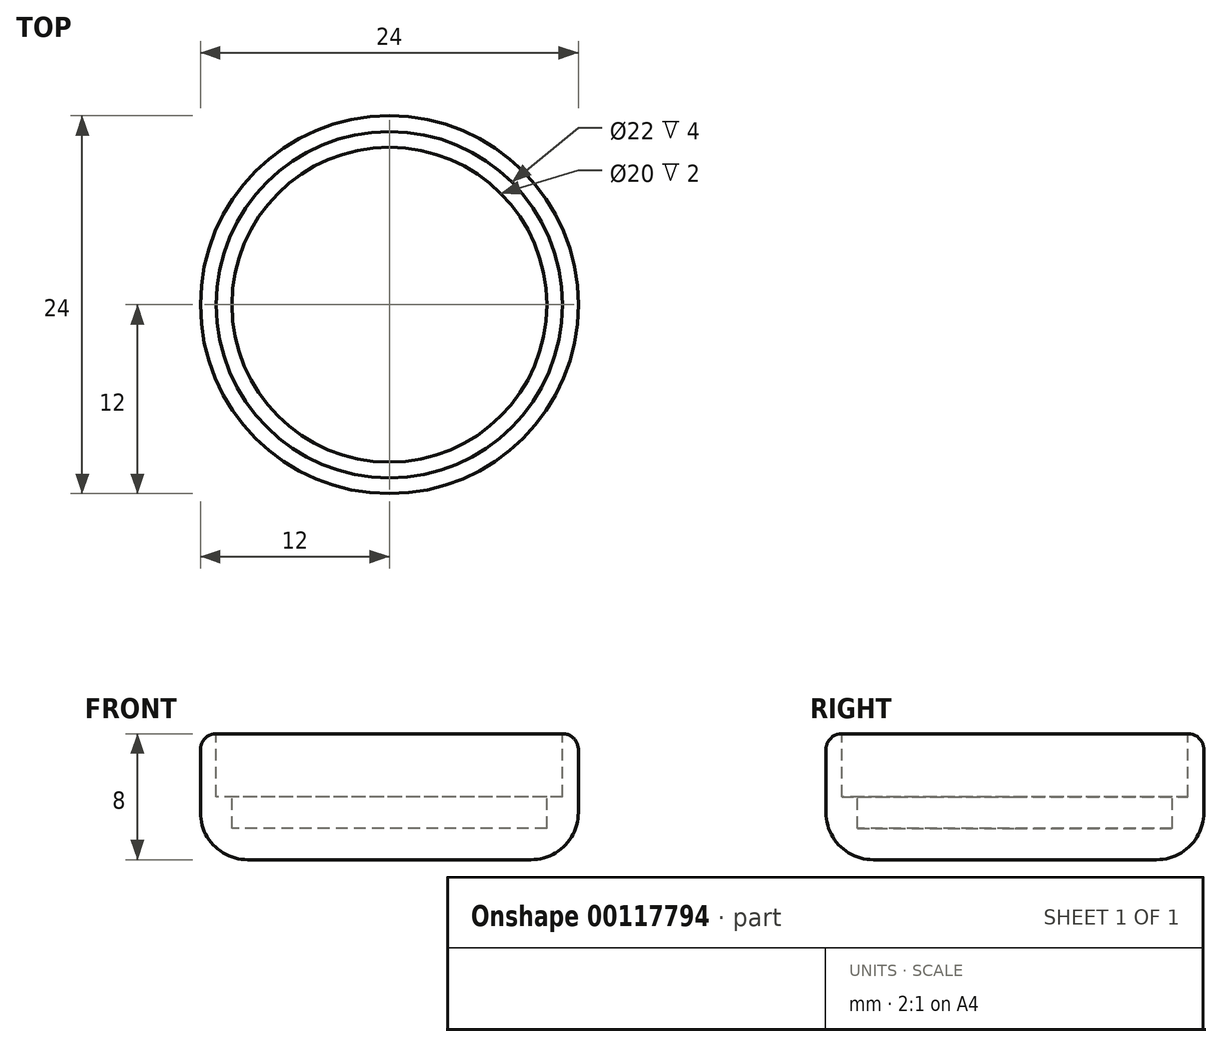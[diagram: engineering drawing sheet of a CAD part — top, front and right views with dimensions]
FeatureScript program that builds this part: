
annotation { "Feature Type Name" : "Feature", "Feature Type Description" : "" }
export const myFeature = defineFeature(function(context is Context, id is Id, definition is map)
    precondition{}
    {
        {
            var Q0;
            Q0=qCreatedBy(makeId("Top.planeOp"),FACE);
            var sketch = newSketch(context, id + "F0", { "sketchPlane" : qUnion([Q0])});
            skCircle(sketch, "E0", {"center": v(0, 0) * mm, "radius": 12 * mm});
            skSolve(sketch);
        }
        {
            var Q0;
            Q0 = qSketchRegion(id + "F0", true);
            extrude(context, id + "F1", {"entities" : qUnion([Q0]), "depth" : 8 * mm});
        }
        {
            var Q0;
            Q0=makeQuery(id+"F1.opExtrude","CAP_FACE",FACE,{"disambiguationData":[OSD([sQuery(id+"F0.wireOp",EDGE,"E0")])],"isStart":false});
            var sketch = newSketch(context, id + "F2", { "sketchPlane" : qUnion([Q0])});
            skCircle(sketch, "E1", {"center": v(0, 0) * mm, "radius": 11 * mm});
            skCircle(sketch, "E2", {"center": v(0, 0) * mm, "radius": 10 * mm});
            skSolve(sketch);
        }
        {
            var Q0;
            Q0=makeQuery(id+"F2.imprint","IMPRINT",FACE,{"disambiguationData":[TD([[makeQuery(id+"F2.imprint","IMPRINT",EDGE,{"derivedFrom":sQuery(id+"F2.wireOp",EDGE,"E2")}),1.0]])]});
            extrude(context, id + "F3", {"entities" : qUnion([Q0]), "operationType" : NewBodyOperationType.REMOVE, "oppositeDirection" : true, "depth" : 6 * mm});
        }
        {
            var Q0;
            Q0 = qSketchRegion(id + "F2", true);
            extrude(context, id + "F4", {"entities" : qUnion([Q0]), "operationType" : NewBodyOperationType.REMOVE, "oppositeDirection" : true, "depth" : 4 * mm});
        }
        {
            var Q0;
            Q0=makeQuery(id+"F1.opExtrude","CAP_EDGE",EDGE,{"disambiguationData":[OSD([sQuery(id+"F0.wireOp",EDGE,"E0")])],"isStart":true});
            fillet(context, id + "F5", {"entities" : qUnion([Q0]), "radius" : 3 * mm, "tangentPropagation" : true, "allowEdgeOverflow" : false});
        }
        {
            var Q0;
            Q0=makeQuery(id+"F1.opExtrude","CAP_EDGE",EDGE,{"disambiguationData":[OSD([sQuery(id+"F0.wireOp",EDGE,"E0")])],"isStart":false});
            fillet(context, id + "F6", {"entities" : qUnion([Q0]), "radius" : 1 * mm, "tangentPropagation" : true, "allowEdgeOverflow" : false});
        }
    });
